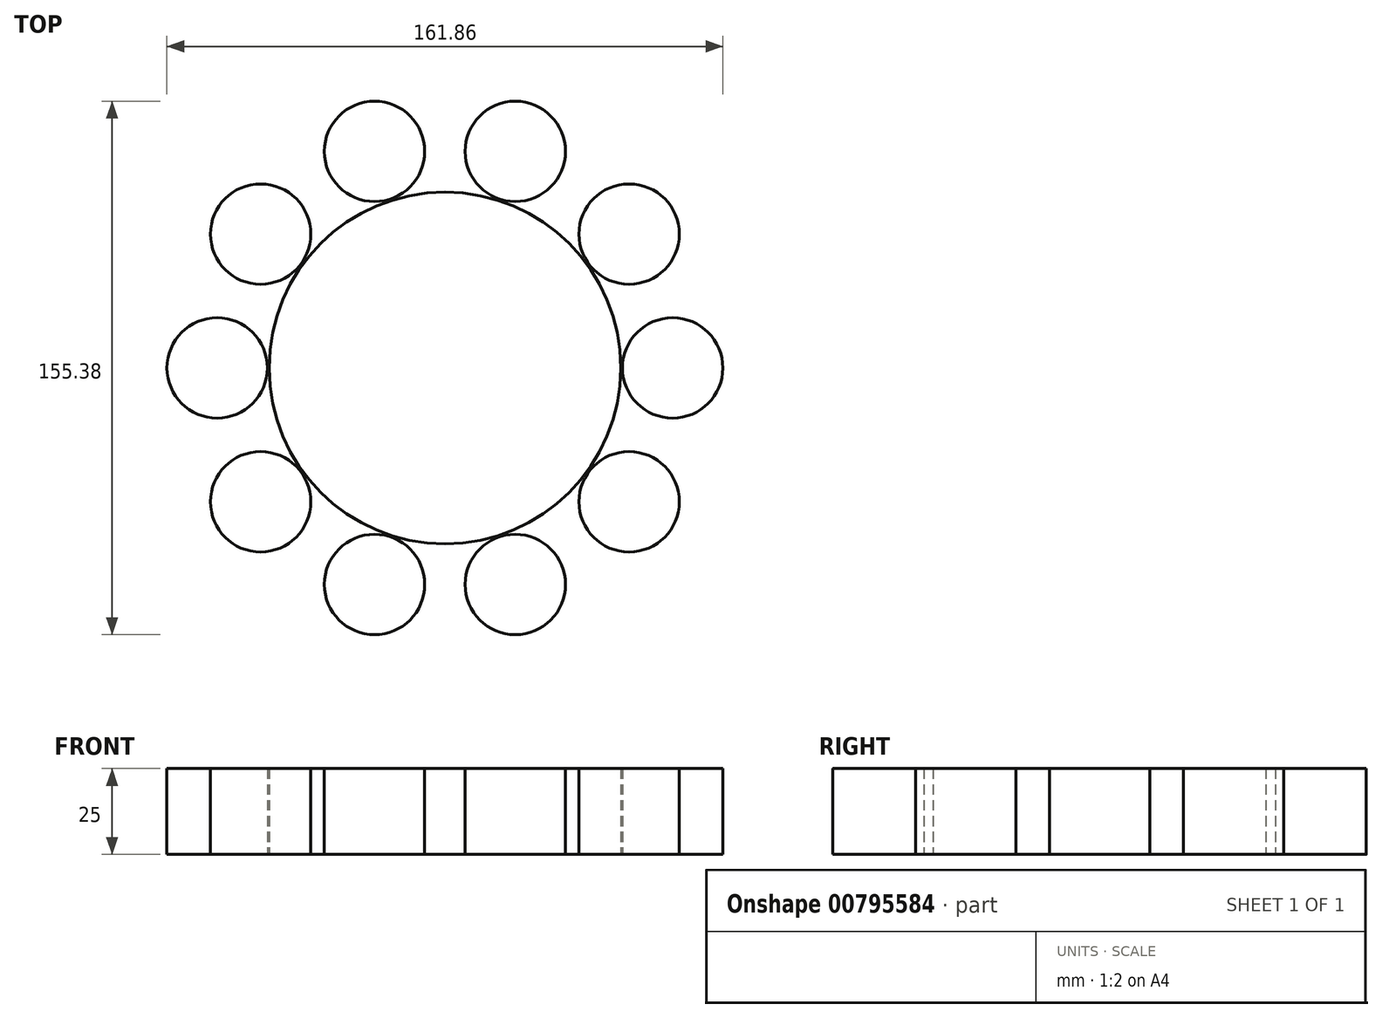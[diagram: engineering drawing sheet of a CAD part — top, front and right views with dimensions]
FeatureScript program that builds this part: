
annotation { "Feature Type Name" : "Feature", "Feature Type Description" : "" }
export const myFeature = defineFeature(function(context is Context, id is Id, definition is map)
    precondition{}
    {
        {
            var Q0;
            Q0=qCreatedBy(makeId("Top.planeOp"),FACE);
            var sketch = newSketch(context, id + "F0", { "sketchPlane" : qUnion([Q0])});
            skCircle(sketch, "E0", {"center": v(0, 0) * mm, "radius": 51.2 * mm});
            skCircle(sketch, "E1", {"center": v(66.32, 0) * mm, "radius": 14.61 * mm});
            skSolve(sketch);
        }
        {
            var Q0;
            Q0=makeQuery(id+"F0.imprint","IMPRINT",FACE,{"disambiguationData":[TD([[makeQuery(id+"F0.imprint","IMPRINT",EDGE,{"derivedFrom":sQuery(id+"F0.wireOp",EDGE,"E0")}),1.0]])]});
            var Q1;
            Q1=makeQuery(id+"F0.imprint","IMPRINT",FACE,{"disambiguationData":[TD([[makeQuery(id+"F0.imprint","IMPRINT",EDGE,{"derivedFrom":sQuery(id+"F0.wireOp",EDGE,"E1")}),1.0]])]});
            extrude(context, id + "F1", {"entities" : qUnion([Q0, Q1]), "depth" : 25 * mm, "offsetDistance" : 25 * mm});
        }
        {
            var Q0;
            Q0=makeQuery(id+"F1.opExtrude","SWEPT_BODY",BODY,{"disambiguationData":[OSD([sQuery(id+"F0.wireOp",EDGE,"E1")])]});
            var Q1;
            Q1=makeQuery(id+"F1.opExtrude","SWEPT_FACE",FACE,{"disambiguationData":[OSD([sQuery(id+"F0.wireOp",EDGE,"E0")])]});
            circularPattern(context, id + "F2", {"entities" : qUnion([Q0]), "axis" : qUnion([Q1]), "angle" : 360 * degree, "instanceCount" : 10, "equalSpace" : true});
        }
    });
